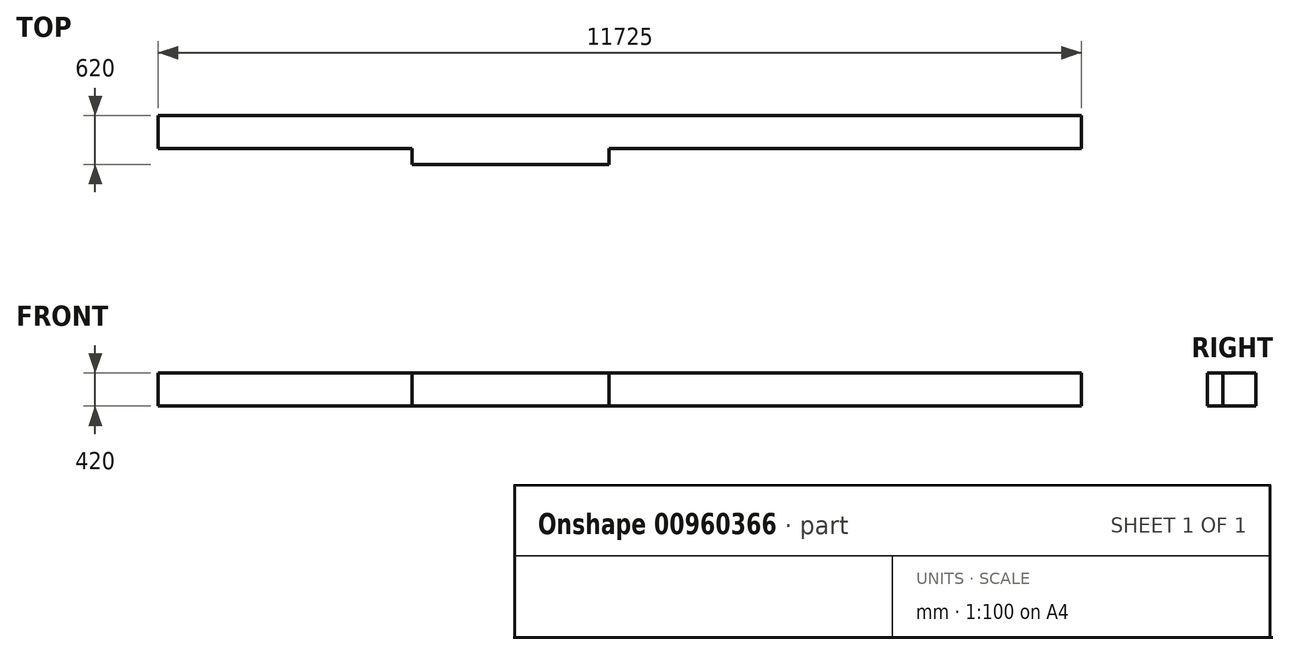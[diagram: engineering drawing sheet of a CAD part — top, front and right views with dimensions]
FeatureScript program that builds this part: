
annotation { "Feature Type Name" : "Feature", "Feature Type Description" : "" }
export const myFeature = defineFeature(function(context is Context, id is Id, definition is map)
    precondition{}
    {
        {
            var Q0;
            Q0=qCreatedBy(makeId("Top.planeOp"),FACE);
            var sketch = newSketch(context, id + "F0", { "sketchPlane" : qUnion([Q0])});
            skLineSegment(sketch, "E0", {"start": v(-62.87, 342.83) * mm, "end": v(-62.87, -77.17) * mm});
            skLineSegment(sketch, "E1", {"start": v(-62.87, -77.17) * mm, "end": v(3162.13, -77.17) * mm});
            skLineSegment(sketch, "E2", {"start": v(-62.87, 342.83) * mm, "end": v(4212.13, 342.83) * mm});
            skLineSegment(sketch, "E3", {"start": v(11662.13, -77.17) * mm, "end": v(11662.13, 342.83) * mm});
            skLineSegment(sketch, "E4", {"start": v(11662.13, 342.83) * mm, "end": v(4212.13, 342.83) * mm});
            skLineSegment(sketch, "E5", {"start": v(3162.13, -77.17) * mm, "end": v(3162.13, -277.17) * mm});
            skLineSegment(sketch, "E6", {"start": v(3162.13, -277.17) * mm, "end": v(5662.13, -277.17) * mm});
            skLineSegment(sketch, "E7", {"start": v(5662.13, -277.17) * mm, "end": v(5662.13, -77.17) * mm});
            skLineSegment(sketch, "E8", {"start": v(5662.13, -77.17) * mm, "end": v(11662.13, -77.17) * mm});
            skSolve(sketch);
        }
        {
            var Q0;
            Q0=makeQuery(id+"F0.imprint","IMPRINT",FACE,{"disambiguationData":[TD([[makeQuery(id+"F0.imprint","IMPRINT",EDGE,{"derivedFrom":sQuery(id+"F0.wireOp",EDGE,"E0")}),1.0]])]});
            extrude(context, id + "F1", {"entities" : qUnion([Q0]), "depth" : 420 * mm, "offsetDistance" : 25 * mm});
        }
    });
